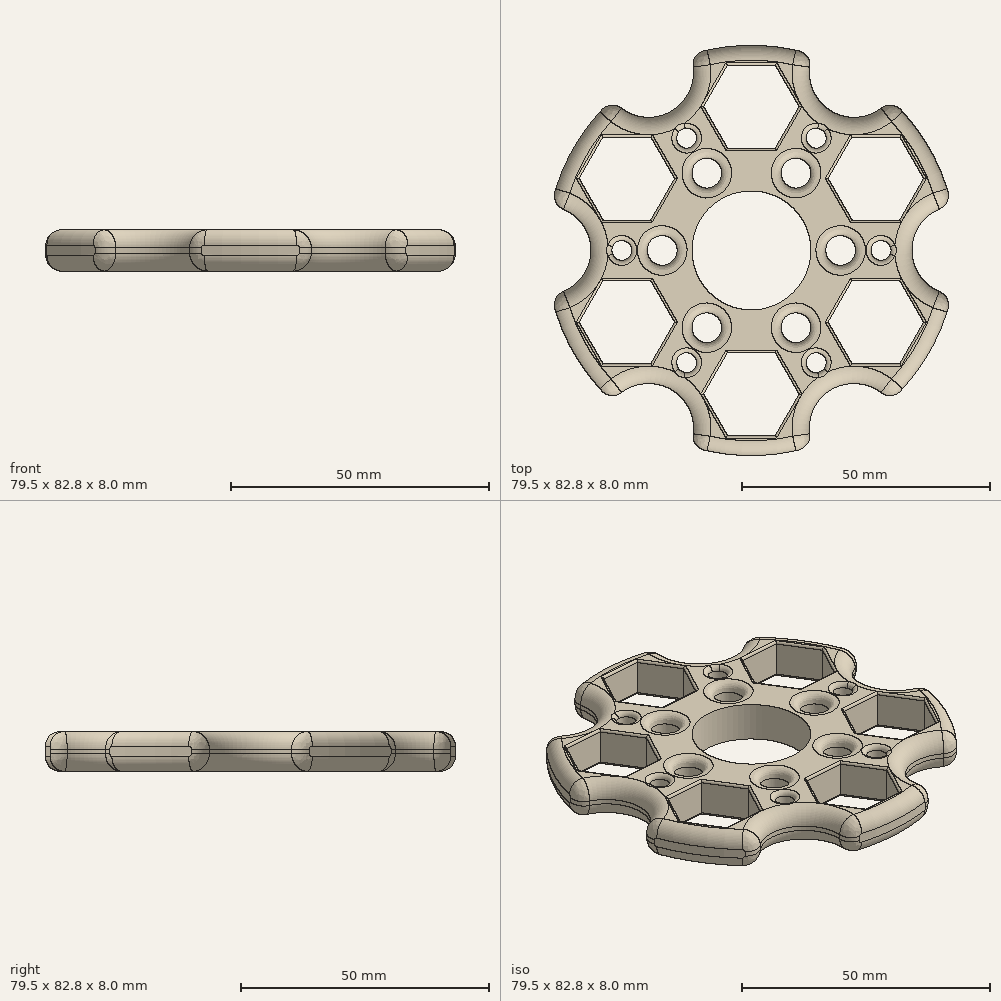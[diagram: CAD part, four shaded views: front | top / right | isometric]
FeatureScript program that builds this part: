
annotation { "Feature Type Name" : "Feature", "Feature Type Description" : "" }
export const myFeature = defineFeature(function(context is Context, id is Id, definition is map)
    precondition{}
    {
        {
            var Q0;
            Q0=qCreatedBy(makeId("Top.planeOp"),FACE);
            var sketch = newSketch(context, id + "F0", { "sketchPlane" : qUnion([Q0])});
            skCircle(sketch, "E0", {"center": v(0, 0) * mm, "radius": 12 * mm});
            skCircle(sketch, "E1", {"center": v(0, 0) * mm, "radius": 41.4 * mm});
            skCircle(sketch, "E2", {"center": v(0, 0) * mm, "radius": 29 * mm});
            skLineSegment(sketch, "E3", {"start": v(0, 0) * mm, "end": v(0, 47.75) * mm});
            skLineSegment(sketch, "E4", {"start": v(0, 0) * mm, "end": v(0, -67.46) * mm});
            skLineSegment(sketch, "E5", {"start": v(0, 0) * mm, "end": v(50.67, 29.25) * mm});
            skLineSegment(sketch, "E6", {"start": v(0, 0) * mm, "end": v(55.86, -32.25) * mm});
            skLineSegment(sketch, "E7", {"start": v(0, 0) * mm, "end": v(-57.52, -33.2) * mm});
            skLineSegment(sketch, "E8", {"start": v(0, 0) * mm, "end": v(-43.6, 25.17) * mm});
            skCircle(sketch, "E9.cCircle", {"center": v(0, 29) * mm, "radius": 8.35 * mm, "construction": true});
            skLineSegment(sketch, "E9.0", {"start": v(4.82, 20.65) * mm, "end": v(-4.82, 20.65) * mm});
            skLineSegment(sketch, "E9.1", {"start": v(-4.82, 20.65) * mm, "end": v(-9.64, 29) * mm});
            skLineSegment(sketch, "E9.2", {"start": v(-9.64, 29) * mm, "end": v(-4.82, 37.35) * mm});
            skLineSegment(sketch, "E9.3", {"start": v(-4.82, 37.35) * mm, "end": v(4.82, 37.35) * mm});
            skLineSegment(sketch, "E9.4", {"start": v(4.82, 37.35) * mm, "end": v(9.64, 29) * mm});
            skLineSegment(sketch, "E9.5", {"start": v(9.64, 29) * mm, "end": v(4.82, 20.65) * mm});
            skPoint(sketch, "E9.0.midPoint", {"position": v(0, 20.65) * mm});
            skCircle(sketch, "E10.cCircle", {"center": v(25.11, 14.5) * mm, "radius": 8.35 * mm, "construction": true});
            skLineSegment(sketch, "E10.0", {"start": v(20.3, 6.15) * mm, "end": v(15.47, 14.5) * mm});
            skLineSegment(sketch, "E10.1", {"start": v(15.47, 14.5) * mm, "end": v(20.3, 22.85) * mm});
            skLineSegment(sketch, "E10.2", {"start": v(20.3, 22.85) * mm, "end": v(29.94, 22.85) * mm});
            skLineSegment(sketch, "E10.3", {"start": v(29.94, 22.85) * mm, "end": v(34.76, 14.5) * mm});
            skLineSegment(sketch, "E10.4", {"start": v(34.76, 14.5) * mm, "end": v(29.94, 6.15) * mm});
            skLineSegment(sketch, "E10.5", {"start": v(29.94, 6.15) * mm, "end": v(20.3, 6.15) * mm});
            skPoint(sketch, "E10.0.midPoint", {"position": v(17.88, 10.33) * mm});
            skCircle(sketch, "E11.cCircle", {"center": v(25.11, -14.5) * mm, "radius": 8.35 * mm, "construction": true});
            skLineSegment(sketch, "E11.0", {"start": v(15.47, -14.5) * mm, "end": v(20.3, -6.15) * mm});
            skLineSegment(sketch, "E11.1", {"start": v(20.3, -6.15) * mm, "end": v(29.94, -6.15) * mm});
            skLineSegment(sketch, "E11.2", {"start": v(29.94, -6.15) * mm, "end": v(34.76, -14.5) * mm});
            skLineSegment(sketch, "E11.3", {"start": v(34.76, -14.5) * mm, "end": v(29.94, -22.85) * mm});
            skLineSegment(sketch, "E11.4", {"start": v(29.94, -22.85) * mm, "end": v(20.3, -22.85) * mm});
            skLineSegment(sketch, "E11.5", {"start": v(20.3, -22.85) * mm, "end": v(15.47, -14.5) * mm});
            skPoint(sketch, "E11.0.midPoint", {"position": v(17.88, -10.32) * mm});
            skCircle(sketch, "E12.cCircle", {"center": v(0, -29) * mm, "radius": 8.35 * mm, "construction": true});
            skLineSegment(sketch, "E12.0", {"start": v(-4.82, -20.65) * mm, "end": v(4.82, -20.65) * mm});
            skLineSegment(sketch, "E12.1", {"start": v(4.82, -20.65) * mm, "end": v(9.64, -29) * mm});
            skLineSegment(sketch, "E12.2", {"start": v(9.64, -29) * mm, "end": v(4.82, -37.35) * mm});
            skLineSegment(sketch, "E12.3", {"start": v(4.82, -37.35) * mm, "end": v(-4.82, -37.35) * mm});
            skLineSegment(sketch, "E12.4", {"start": v(-4.82, -37.35) * mm, "end": v(-9.64, -29) * mm});
            skLineSegment(sketch, "E12.5", {"start": v(-9.64, -29) * mm, "end": v(-4.82, -20.65) * mm});
            skPoint(sketch, "E12.0.midPoint", {"position": v(0, -20.65) * mm});
            skCircle(sketch, "E13.cCircle", {"center": v(-25.11, -14.5) * mm, "radius": 8.35 * mm, "construction": true});
            skLineSegment(sketch, "E13.0", {"start": v(-20.3, -6.15) * mm, "end": v(-15.47, -14.5) * mm});
            skLineSegment(sketch, "E13.1", {"start": v(-15.47, -14.5) * mm, "end": v(-20.3, -22.85) * mm});
            skLineSegment(sketch, "E13.2", {"start": v(-20.3, -22.85) * mm, "end": v(-29.94, -22.85) * mm});
            skLineSegment(sketch, "E13.3", {"start": v(-29.94, -22.85) * mm, "end": v(-34.76, -14.5) * mm});
            skLineSegment(sketch, "E13.4", {"start": v(-34.76, -14.5) * mm, "end": v(-29.94, -6.15) * mm});
            skLineSegment(sketch, "E13.5", {"start": v(-29.94, -6.15) * mm, "end": v(-20.3, -6.15) * mm});
            skPoint(sketch, "E13.0.midPoint", {"position": v(-17.88, -10.33) * mm});
            skCircle(sketch, "E14.cCircle", {"center": v(-25.11, 14.5) * mm, "radius": 8.35 * mm, "construction": true});
            skLineSegment(sketch, "E14.0", {"start": v(-15.47, 14.5) * mm, "end": v(-20.3, 6.15) * mm});
            skLineSegment(sketch, "E14.1", {"start": v(-20.3, 6.15) * mm, "end": v(-29.94, 6.15) * mm});
            skLineSegment(sketch, "E14.2", {"start": v(-29.94, 6.15) * mm, "end": v(-34.76, 14.5) * mm});
            skLineSegment(sketch, "E14.3", {"start": v(-34.76, 14.5) * mm, "end": v(-29.94, 22.85) * mm});
            skLineSegment(sketch, "E14.4", {"start": v(-29.94, 22.85) * mm, "end": v(-20.3, 22.85) * mm});
            skLineSegment(sketch, "E14.5", {"start": v(-20.3, 22.85) * mm, "end": v(-15.47, 14.5) * mm});
            skPoint(sketch, "E14.0.midPoint", {"position": v(-17.88, 10.32) * mm});
            skLineSegment(sketch, "E15", {"start": v(0, 0) * mm, "end": v(-28.15, -48.76) * mm});
            skLineSegment(sketch, "E16", {"start": v(0, 0) * mm, "end": v(-26.9, 46.6) * mm});
            skLineSegment(sketch, "E17", {"start": v(0, 0) * mm, "end": v(-57.79, 0) * mm});
            skLineSegment(sketch, "E18", {"start": v(0, 0) * mm, "end": v(54.8, 0) * mm});
            skLineSegment(sketch, "E19", {"start": v(0, 0) * mm, "end": v(27, -46.77) * mm});
            skLineSegment(sketch, "E20", {"start": v(0, 0) * mm, "end": v(25.69, 44.49) * mm});
            skCircle(sketch, "E21", {"center": v(-20.7, 35.85) * mm, "radius": 9 * mm});
            skCircle(sketch, "E22", {"center": v(41.4, 0) * mm, "radius": 9 * mm});
            skCircle(sketch, "E23", {"center": v(20.7, 35.85) * mm, "radius": 9 * mm});
            skCircle(sketch, "E24", {"center": v(20.7, -35.85) * mm, "radius": 9 * mm});
            skCircle(sketch, "E25", {"center": v(-20.7, -35.85) * mm, "radius": 9 * mm});
            skCircle(sketch, "E26", {"center": v(-41.4, 0) * mm, "radius": 9 * mm});
            skCircle(sketch, "E27", {"center": v(0, 0) * mm, "radius": 18 * mm});
            skCircle(sketch, "E28", {"center": v(-18, 0) * mm, "radius": 3 * mm});
            skCircle(sketch, "E29", {"center": v(-9, 15.59) * mm, "radius": 3 * mm});
            skCircle(sketch, "E30", {"center": v(9, 15.59) * mm, "radius": 3 * mm});
            skCircle(sketch, "E31", {"center": v(18, 0) * mm, "radius": 3 * mm});
            skCircle(sketch, "E32", {"center": v(9, -15.59) * mm, "radius": 3 * mm});
            skCircle(sketch, "E33", {"center": v(-9, -15.59) * mm, "radius": 3 * mm});
            skCircle(sketch, "E34", {"center": v(0, 0) * mm, "radius": 26.15 * mm});
            skCircle(sketch, "E35", {"center": v(-13.08, -22.65) * mm, "radius": 2 * mm});
            skCircle(sketch, "E36", {"center": v(13.08, -22.65) * mm, "radius": 2 * mm});
            skCircle(sketch, "E37", {"center": v(26.15, 0) * mm, "radius": 2 * mm});
            skCircle(sketch, "E38", {"center": v(13.08, 22.65) * mm, "radius": 2 * mm});
            skCircle(sketch, "E39", {"center": v(-13.08, 22.65) * mm, "radius": 2 * mm});
            skCircle(sketch, "E40", {"center": v(-26.15, 0) * mm, "radius": 2 * mm});
            skSolve(sketch);
        }
        {
            var Q0;
            {var subQ0=sQuery(id+"F0.wireOp",EDGE,"E10.4");Q0=makeQuery(id+"F0.imprint","IMPRINT",FACE,{"disambiguationData":[TD([[makeQuery(id+"F0.imprint","IMPRINT",EDGE,{"derivedFrom":subQ0}),1.0]])]});}
            var Q1;
            {var subQ5=sQuery(id+"F0.wireOp",EDGE,"E10.2");Q1=makeQuery(id+"F0.imprint","IMPRINT",FACE,{"disambiguationData":[TD([[makeQuery(id+"F0.imprint","IMPRINT",EDGE,{"derivedFrom":subQ5}),1.0]])]});}
            var Q2;
            {var subQ10=sQuery(id+"F0.wireOp",EDGE,"E9.4");Q2=makeQuery(id+"F0.imprint","IMPRINT",FACE,{"disambiguationData":[TD([[makeQuery(id+"F0.imprint","IMPRINT",EDGE,{"derivedFrom":subQ10}),1.0]])]});}
            var Q3;
            {var subQ0=sQuery(id+"F0.wireOp",EDGE,"E9.2");Q3=makeQuery(id+"F0.imprint","IMPRINT",FACE,{"disambiguationData":[TD([[makeQuery(id+"F0.imprint","IMPRINT",EDGE,{"derivedFrom":subQ0}),1.0]])]});}
            var Q4;
            {var subQ0=sQuery(id+"F0.wireOp",EDGE,"E14.4");Q4=makeQuery(id+"F0.imprint","IMPRINT",FACE,{"disambiguationData":[TD([[makeQuery(id+"F0.imprint","IMPRINT",EDGE,{"derivedFrom":subQ0}),1.0]])]});}
            var Q5;
            {var subQ0=sQuery(id+"F0.wireOp",EDGE,"E14.2");Q5=makeQuery(id+"F0.imprint","IMPRINT",FACE,{"disambiguationData":[TD([[makeQuery(id+"F0.imprint","IMPRINT",EDGE,{"derivedFrom":subQ0}),1.0]])]});}
            var Q6;
            {var subQ0=sQuery(id+"F0.wireOp",EDGE,"E13.4");Q6=makeQuery(id+"F0.imprint","IMPRINT",FACE,{"disambiguationData":[TD([[makeQuery(id+"F0.imprint","IMPRINT",EDGE,{"derivedFrom":subQ0}),1.0]])]});}
            var Q7;
            {var subQ0=sQuery(id+"F0.wireOp",EDGE,"E13.2");Q7=makeQuery(id+"F0.imprint","IMPRINT",FACE,{"disambiguationData":[TD([[makeQuery(id+"F0.imprint","IMPRINT",EDGE,{"derivedFrom":subQ0}),1.0]])]});}
            var Q8;
            {var subQ5=sQuery(id+"F0.wireOp",EDGE,"E12.4");Q8=makeQuery(id+"F0.imprint","IMPRINT",FACE,{"disambiguationData":[TD([[makeQuery(id+"F0.imprint","IMPRINT",EDGE,{"derivedFrom":subQ5}),1.0]])]});}
            var Q9;
            {var subQ0=sQuery(id+"F0.wireOp",EDGE,"E12.2");Q9=makeQuery(id+"F0.imprint","IMPRINT",FACE,{"disambiguationData":[TD([[makeQuery(id+"F0.imprint","IMPRINT",EDGE,{"derivedFrom":subQ0}),1.0]])]});}
            var Q10;
            {var subQ0=sQuery(id+"F0.wireOp",EDGE,"E11.4");Q10=makeQuery(id+"F0.imprint","IMPRINT",FACE,{"disambiguationData":[TD([[makeQuery(id+"F0.imprint","IMPRINT",EDGE,{"derivedFrom":subQ0}),1.0]])]});}
            var Q11;
            {var subQ5=sQuery(id+"F0.wireOp",EDGE,"E11.2");Q11=makeQuery(id+"F0.imprint","IMPRINT",FACE,{"disambiguationData":[TD([[makeQuery(id+"F0.imprint","IMPRINT",EDGE,{"derivedFrom":subQ5}),1.0]])]});}
            var Q12;
            {var subQ0=sQuery(id+"F0.wireOp",EDGE,"E17");var subQ1=sQuery(id+"F0.wireOp",EDGE,"E0");var subQ2=makeQuery(id+"F0.imprint","INTERSECT",VERTEX,{"derivedFrom":[subQ1,subQ0]});Q12=makeQuery(id+"F0.imprint","IMPRINT",FACE,{"disambiguationData":[TD([[makeQuery(id+"F0.imprint","IMPRINT",EDGE,{"disambiguationData":[TD([[subQ2,-1.0]])],"derivedFrom":subQ1}),-1.0]])]});}
            var Q13;
            {var subQ5=sQuery(id+"F0.wireOp",EDGE,"E16");var subQ6=sQuery(id+"F0.wireOp",EDGE,"E0");var subQ7=makeQuery(id+"F0.imprint","INTERSECT",VERTEX,{"derivedFrom":[subQ6,subQ5]});Q13=makeQuery(id+"F0.imprint","IMPRINT",FACE,{"disambiguationData":[TD([[makeQuery(id+"F0.imprint","IMPRINT",EDGE,{"disambiguationData":[TD([[subQ7,-1.0]])],"derivedFrom":subQ6}),-1.0]])]});}
            var Q14;
            {var subQ1=sQuery(id+"F0.wireOp",EDGE,"E8");var subQ6=sQuery(id+"F0.wireOp",EDGE,"E0");var subQ9=makeQuery(id+"F0.imprint","INTERSECT",VERTEX,{"derivedFrom":[subQ6,subQ1]});Q14=makeQuery(id+"F0.imprint","IMPRINT",FACE,{"disambiguationData":[TD([[makeQuery(id+"F0.imprint","IMPRINT",EDGE,{"disambiguationData":[TD([[subQ9,-1.0]])],"derivedFrom":subQ6}),-1.0]])]});}
            var Q15;
            {var subQ3=sQuery(id+"F0.wireOp",EDGE,"E2");var subQ7=sQuery(id+"F0.wireOp",EDGE,"E16");var subQ8=makeQuery(id+"F0.imprint","INTERSECT",VERTEX,{"derivedFrom":[subQ3,subQ7]});Q15=makeQuery(id+"F0.imprint","IMPRINT",FACE,{"disambiguationData":[TD([[makeQuery(id+"F0.imprint","IMPRINT",EDGE,{"disambiguationData":[TD([[subQ8,-1.0]])],"derivedFrom":subQ3}),1.0]])]});}
            var Q16;
            {var subQ0=sQuery(id+"F0.wireOp",EDGE,"E9.1");var subQ7=sQuery(id+"F0.wireOp",EDGE,"E2");var subQ8=makeQuery(id+"F0.imprint","INTERSECT",VERTEX,{"derivedFrom":[subQ7,subQ0]});Q16=makeQuery(id+"F0.imprint","IMPRINT",FACE,{"disambiguationData":[TD([[makeQuery(id+"F0.imprint","IMPRINT",EDGE,{"disambiguationData":[TD([[subQ8,-1.0]])],"derivedFrom":subQ7}),1.0]])]});}
            var Q17;
            {var subQ1=sQuery(id+"F0.wireOp",EDGE,"E3");var subQ5=sQuery(id+"F0.wireOp",EDGE,"E0");var subQ6=makeQuery(id+"F0.imprint","INTERSECT",VERTEX,{"derivedFrom":[subQ5,subQ1]});Q17=makeQuery(id+"F0.imprint","IMPRINT",FACE,{"disambiguationData":[TD([[makeQuery(id+"F0.imprint","IMPRINT",EDGE,{"disambiguationData":[TD([[subQ6,-1.0]])],"derivedFrom":subQ5}),-1.0]])]});}
            var Q18;
            {var subQ5=sQuery(id+"F0.wireOp",EDGE,"E20");var subQ6=sQuery(id+"F0.wireOp",EDGE,"E0");var subQ7=makeQuery(id+"F0.imprint","INTERSECT",VERTEX,{"derivedFrom":[subQ6,subQ5]});Q18=makeQuery(id+"F0.imprint","IMPRINT",FACE,{"disambiguationData":[TD([[makeQuery(id+"F0.imprint","IMPRINT",EDGE,{"disambiguationData":[TD([[subQ7,-1.0]])],"derivedFrom":subQ6}),-1.0]])]});}
            var Q19;
            {var subQ7=sQuery(id+"F0.wireOp",EDGE,"E20");var subQ8=sQuery(id+"F0.wireOp",EDGE,"E2");var subQ9=makeQuery(id+"F0.imprint","INTERSECT",VERTEX,{"derivedFrom":[subQ8,subQ7]});Q19=makeQuery(id+"F0.imprint","IMPRINT",FACE,{"disambiguationData":[TD([[makeQuery(id+"F0.imprint","IMPRINT",EDGE,{"disambiguationData":[TD([[subQ9,-1.0]])],"derivedFrom":subQ8}),1.0]])]});}
            var Q20;
            {var subQ0=sQuery(id+"F0.wireOp",EDGE,"E10.1");var subQ3=sQuery(id+"F0.wireOp",EDGE,"E2");var subQ4=makeQuery(id+"F0.imprint","INTERSECT",VERTEX,{"derivedFrom":[subQ3,subQ0]});Q20=makeQuery(id+"F0.imprint","IMPRINT",FACE,{"disambiguationData":[TD([[makeQuery(id+"F0.imprint","IMPRINT",EDGE,{"disambiguationData":[TD([[subQ4,-1.0]])],"derivedFrom":subQ3}),1.0]])]});}
            var Q21;
            {var subQ1=sQuery(id+"F0.wireOp",EDGE,"E5");var subQ6=sQuery(id+"F0.wireOp",EDGE,"E0");var subQ9=makeQuery(id+"F0.imprint","INTERSECT",VERTEX,{"derivedFrom":[subQ6,subQ1]});Q21=makeQuery(id+"F0.imprint","IMPRINT",FACE,{"disambiguationData":[TD([[makeQuery(id+"F0.imprint","IMPRINT",EDGE,{"disambiguationData":[TD([[subQ9,-1.0]])],"derivedFrom":subQ6}),-1.0]])]});}
            var Q22;
            {var subQ1=sQuery(id+"F0.wireOp",EDGE,"E5");var subQ6=sQuery(id+"F0.wireOp",EDGE,"E0");var subQ9=makeQuery(id+"F0.imprint","INTERSECT",VERTEX,{"derivedFrom":[subQ6,subQ1]});Q22=makeQuery(id+"F0.imprint","IMPRINT",FACE,{"disambiguationData":[TD([[makeQuery(id+"F0.imprint","IMPRINT",EDGE,{"disambiguationData":[TD([[subQ9,1.0]])],"derivedFrom":subQ6}),-1.0]])]});}
            var Q23;
            {var subQ5=sQuery(id+"F0.wireOp",EDGE,"E0");var subQ7=sQuery(id+"F0.wireOp",EDGE,"E18");var subQ9=makeQuery(id+"F0.imprint","INTERSECT",VERTEX,{"derivedFrom":[subQ5,subQ7]});Q23=makeQuery(id+"F0.imprint","IMPRINT",FACE,{"disambiguationData":[TD([[makeQuery(id+"F0.imprint","IMPRINT",EDGE,{"disambiguationData":[TD([[subQ9,1.0]])],"derivedFrom":subQ5}),-1.0]])]});}
            var Q24;
            {var subQ5=sQuery(id+"F0.wireOp",EDGE,"E19");var subQ6=sQuery(id+"F0.wireOp",EDGE,"E0");var subQ7=makeQuery(id+"F0.imprint","INTERSECT",VERTEX,{"derivedFrom":[subQ6,subQ5]});Q24=makeQuery(id+"F0.imprint","IMPRINT",FACE,{"disambiguationData":[TD([[makeQuery(id+"F0.imprint","IMPRINT",EDGE,{"disambiguationData":[TD([[subQ7,-1.0]])],"derivedFrom":subQ6}),-1.0]])]});}
            var Q25;
            {var subQ1=sQuery(id+"F0.wireOp",EDGE,"E4");var subQ5=sQuery(id+"F0.wireOp",EDGE,"E0");var subQ6=makeQuery(id+"F0.imprint","INTERSECT",VERTEX,{"derivedFrom":[subQ5,subQ1]});Q25=makeQuery(id+"F0.imprint","IMPRINT",FACE,{"disambiguationData":[TD([[makeQuery(id+"F0.imprint","IMPRINT",EDGE,{"disambiguationData":[TD([[subQ6,-1.0]])],"derivedFrom":subQ5}),-1.0]])]});}
            var Q26;
            {var subQ5=sQuery(id+"F0.wireOp",EDGE,"E15");var subQ6=sQuery(id+"F0.wireOp",EDGE,"E0");var subQ7=makeQuery(id+"F0.imprint","INTERSECT",VERTEX,{"derivedFrom":[subQ6,subQ5]});Q26=makeQuery(id+"F0.imprint","IMPRINT",FACE,{"disambiguationData":[TD([[makeQuery(id+"F0.imprint","IMPRINT",EDGE,{"disambiguationData":[TD([[subQ7,-1.0]])],"derivedFrom":subQ6}),-1.0]])]});}
            var Q27;
            {var subQ0=sQuery(id+"F0.wireOp",EDGE,"E7");var subQ1=sQuery(id+"F0.wireOp",EDGE,"E0");var subQ2=makeQuery(id+"F0.imprint","INTERSECT",VERTEX,{"derivedFrom":[subQ1,subQ0]});Q27=makeQuery(id+"F0.imprint","IMPRINT",FACE,{"disambiguationData":[TD([[makeQuery(id+"F0.imprint","IMPRINT",EDGE,{"disambiguationData":[TD([[subQ2,-1.0]])],"derivedFrom":subQ1}),-1.0]])]});}
            var Q28;
            {var subQ0=sQuery(id+"F0.wireOp",EDGE,"E13.1");var subQ3=sQuery(id+"F0.wireOp",EDGE,"E2");var subQ4=makeQuery(id+"F0.imprint","INTERSECT",VERTEX,{"derivedFrom":[subQ3,subQ0]});Q28=makeQuery(id+"F0.imprint","IMPRINT",FACE,{"disambiguationData":[TD([[makeQuery(id+"F0.imprint","IMPRINT",EDGE,{"disambiguationData":[TD([[subQ4,-1.0]])],"derivedFrom":subQ3}),1.0]])]});}
            var Q29;
            {var subQ3=sQuery(id+"F0.wireOp",EDGE,"E2");var subQ11=sQuery(id+"F0.wireOp",EDGE,"E15");var subQ12=makeQuery(id+"F0.imprint","INTERSECT",VERTEX,{"derivedFrom":[subQ3,subQ11]});Q29=makeQuery(id+"F0.imprint","IMPRINT",FACE,{"disambiguationData":[TD([[makeQuery(id+"F0.imprint","IMPRINT",EDGE,{"disambiguationData":[TD([[subQ12,-1.0]])],"derivedFrom":subQ3}),1.0]])]});}
            var Q30;
            {var subQ0=sQuery(id+"F0.wireOp",EDGE,"E12.1");var subQ10=sQuery(id+"F0.wireOp",EDGE,"E2");var subQ11=makeQuery(id+"F0.imprint","INTERSECT",VERTEX,{"derivedFrom":[subQ10,subQ0]});Q30=makeQuery(id+"F0.imprint","IMPRINT",FACE,{"disambiguationData":[TD([[makeQuery(id+"F0.imprint","IMPRINT",EDGE,{"disambiguationData":[TD([[subQ11,-1.0]])],"derivedFrom":subQ10}),1.0]])]});}
            var Q31;
            {var subQ3=sQuery(id+"F0.wireOp",EDGE,"E2");var subQ9=sQuery(id+"F0.wireOp",EDGE,"E19");var subQ10=makeQuery(id+"F0.imprint","INTERSECT",VERTEX,{"derivedFrom":[subQ3,subQ9]});Q31=makeQuery(id+"F0.imprint","IMPRINT",FACE,{"disambiguationData":[TD([[makeQuery(id+"F0.imprint","IMPRINT",EDGE,{"disambiguationData":[TD([[subQ10,-1.0]])],"derivedFrom":subQ3}),1.0]])]});}
            var Q32;
            {var subQ3=sQuery(id+"F0.wireOp",EDGE,"E2");var subQ5=sQuery(id+"F0.wireOp",EDGE,"E18");var subQ6=makeQuery(id+"F0.imprint","INTERSECT",VERTEX,{"derivedFrom":[subQ3,subQ5]});Q32=makeQuery(id+"F0.imprint","IMPRINT",FACE,{"disambiguationData":[TD([[makeQuery(id+"F0.imprint","IMPRINT",EDGE,{"disambiguationData":[TD([[subQ6,1.0]])],"derivedFrom":subQ3}),1.0]])]});}
            var Q33;
            {var subQ0=sQuery(id+"F0.wireOp",EDGE,"E10.5");var subQ3=sQuery(id+"F0.wireOp",EDGE,"E2");var subQ4=makeQuery(id+"F0.imprint","INTERSECT",VERTEX,{"derivedFrom":[subQ3,subQ0]});Q33=makeQuery(id+"F0.imprint","IMPRINT",FACE,{"disambiguationData":[TD([[makeQuery(id+"F0.imprint","IMPRINT",EDGE,{"disambiguationData":[TD([[subQ4,1.0]])],"derivedFrom":subQ3}),1.0]])]});}
            var Q34;
            {var subQ3=sQuery(id+"F0.wireOp",EDGE,"E2");var subQ7=sQuery(id+"F0.wireOp",EDGE,"E17");var subQ8=makeQuery(id+"F0.imprint","INTERSECT",VERTEX,{"derivedFrom":[subQ3,subQ7]});Q34=makeQuery(id+"F0.imprint","IMPRINT",FACE,{"disambiguationData":[TD([[makeQuery(id+"F0.imprint","IMPRINT",EDGE,{"disambiguationData":[TD([[subQ8,-1.0]])],"derivedFrom":subQ3}),1.0]])]});}
            var Q35;
            {var subQ0=sQuery(id+"F0.wireOp",EDGE,"E14.1");var subQ3=sQuery(id+"F0.wireOp",EDGE,"E2");var subQ4=makeQuery(id+"F0.imprint","INTERSECT",VERTEX,{"derivedFrom":[subQ3,subQ0]});Q35=makeQuery(id+"F0.imprint","IMPRINT",FACE,{"disambiguationData":[TD([[makeQuery(id+"F0.imprint","IMPRINT",EDGE,{"disambiguationData":[TD([[subQ4,-1.0]])],"derivedFrom":subQ3}),1.0]])]});}
            var Q36;
            {var subQ5=sQuery(id+"F0.wireOp",EDGE,"E27");var subQ6=sQuery(id+"F0.wireOp",EDGE,"E7");var subQ7=makeQuery(id+"F0.imprint","INTERSECT",VERTEX,{"derivedFrom":[subQ6,subQ5]});Q36=makeQuery(id+"F0.imprint","IMPRINT",FACE,{"disambiguationData":[TD([[makeQuery(id+"F0.imprint","IMPRINT",EDGE,{"disambiguationData":[TD([[subQ7,-1.0]])],"derivedFrom":subQ6}),1.0]])]});}
            var Q37;
            {var subQ5=sQuery(id+"F0.wireOp",EDGE,"E27");var subQ10=sQuery(id+"F0.wireOp",EDGE,"E4");var subQ14=makeQuery(id+"F0.imprint","INTERSECT",VERTEX,{"derivedFrom":[subQ10,subQ5]});Q37=makeQuery(id+"F0.imprint","IMPRINT",FACE,{"disambiguationData":[TD([[makeQuery(id+"F0.imprint","IMPRINT",EDGE,{"disambiguationData":[TD([[subQ14,-1.0]])],"derivedFrom":subQ10}),-1.0]])]});}
            var Q38;
            {var subQ11=sQuery(id+"F0.wireOp",EDGE,"E6");var subQ13=sQuery(id+"F0.wireOp",EDGE,"E27");var subQ14=makeQuery(id+"F0.imprint","INTERSECT",VERTEX,{"derivedFrom":[subQ11,subQ13]});Q38=makeQuery(id+"F0.imprint","IMPRINT",FACE,{"disambiguationData":[TD([[makeQuery(id+"F0.imprint","IMPRINT",EDGE,{"disambiguationData":[TD([[subQ14,-1.0]])],"derivedFrom":subQ11}),-1.0]])]});}
            var Q39;
            {var subQ8=sQuery(id+"F0.wireOp",EDGE,"E6");var subQ10=sQuery(id+"F0.wireOp",EDGE,"E27");var subQ11=makeQuery(id+"F0.imprint","INTERSECT",VERTEX,{"derivedFrom":[subQ8,subQ10]});Q39=makeQuery(id+"F0.imprint","IMPRINT",FACE,{"disambiguationData":[TD([[makeQuery(id+"F0.imprint","IMPRINT",EDGE,{"disambiguationData":[TD([[subQ11,-1.0]])],"derivedFrom":subQ8}),1.0]])]});}
            var Q40;
            {var subQ5=sQuery(id+"F0.wireOp",EDGE,"E5");var subQ12=sQuery(id+"F0.wireOp",EDGE,"E27");var subQ13=makeQuery(id+"F0.imprint","INTERSECT",VERTEX,{"derivedFrom":[subQ5,subQ12]});Q40=makeQuery(id+"F0.imprint","IMPRINT",FACE,{"disambiguationData":[TD([[makeQuery(id+"F0.imprint","IMPRINT",EDGE,{"disambiguationData":[TD([[subQ13,-1.0]])],"derivedFrom":subQ5}),-1.0]])]});}
            var Q41;
            {var subQ5=sQuery(id+"F0.wireOp",EDGE,"E27");var subQ6=sQuery(id+"F0.wireOp",EDGE,"E5");var subQ7=makeQuery(id+"F0.imprint","INTERSECT",VERTEX,{"derivedFrom":[subQ6,subQ5]});Q41=makeQuery(id+"F0.imprint","IMPRINT",FACE,{"disambiguationData":[TD([[makeQuery(id+"F0.imprint","IMPRINT",EDGE,{"disambiguationData":[TD([[subQ7,-1.0]])],"derivedFrom":subQ6}),1.0]])]});}
            var Q42;
            {var subQ10=sQuery(id+"F0.wireOp",EDGE,"E3");var subQ12=sQuery(id+"F0.wireOp",EDGE,"E27");var subQ13=makeQuery(id+"F0.imprint","INTERSECT",VERTEX,{"derivedFrom":[subQ10,subQ12]});Q42=makeQuery(id+"F0.imprint","IMPRINT",FACE,{"disambiguationData":[TD([[makeQuery(id+"F0.imprint","IMPRINT",EDGE,{"disambiguationData":[TD([[subQ13,-1.0]])],"derivedFrom":subQ10}),-1.0]])]});}
            var Q43;
            {var subQ10=sQuery(id+"F0.wireOp",EDGE,"E3");var subQ13=sQuery(id+"F0.wireOp",EDGE,"E27");var subQ14=makeQuery(id+"F0.imprint","INTERSECT",VERTEX,{"derivedFrom":[subQ10,subQ13]});Q43=makeQuery(id+"F0.imprint","IMPRINT",FACE,{"disambiguationData":[TD([[makeQuery(id+"F0.imprint","IMPRINT",EDGE,{"disambiguationData":[TD([[subQ14,-1.0]])],"derivedFrom":subQ10}),1.0]])]});}
            var Q44;
            {var subQ10=sQuery(id+"F0.wireOp",EDGE,"E8");var subQ12=sQuery(id+"F0.wireOp",EDGE,"E27");var subQ13=makeQuery(id+"F0.imprint","INTERSECT",VERTEX,{"derivedFrom":[subQ10,subQ12]});Q44=makeQuery(id+"F0.imprint","IMPRINT",FACE,{"disambiguationData":[TD([[makeQuery(id+"F0.imprint","IMPRINT",EDGE,{"disambiguationData":[TD([[subQ13,-1.0]])],"derivedFrom":subQ10}),-1.0]])]});}
            var Q45;
            {var subQ10=sQuery(id+"F0.wireOp",EDGE,"E27");var subQ11=sQuery(id+"F0.wireOp",EDGE,"E8");var subQ12=makeQuery(id+"F0.imprint","INTERSECT",VERTEX,{"derivedFrom":[subQ11,subQ10]});Q45=makeQuery(id+"F0.imprint","IMPRINT",FACE,{"disambiguationData":[TD([[makeQuery(id+"F0.imprint","IMPRINT",EDGE,{"disambiguationData":[TD([[subQ12,-1.0]])],"derivedFrom":subQ11}),1.0]])]});}
            var Q46;
            {var subQ5=sQuery(id+"F0.wireOp",EDGE,"E7");var subQ12=sQuery(id+"F0.wireOp",EDGE,"E27");var subQ13=makeQuery(id+"F0.imprint","INTERSECT",VERTEX,{"derivedFrom":[subQ5,subQ12]});Q46=makeQuery(id+"F0.imprint","IMPRINT",FACE,{"disambiguationData":[TD([[makeQuery(id+"F0.imprint","IMPRINT",EDGE,{"disambiguationData":[TD([[subQ13,-1.0]])],"derivedFrom":subQ5}),-1.0]])]});}
            var Q47;
            {var subQ10=sQuery(id+"F0.wireOp",EDGE,"E4");var subQ12=sQuery(id+"F0.wireOp",EDGE,"E27");var subQ13=makeQuery(id+"F0.imprint","INTERSECT",VERTEX,{"derivedFrom":[subQ10,subQ12]});Q47=makeQuery(id+"F0.imprint","IMPRINT",FACE,{"disambiguationData":[TD([[makeQuery(id+"F0.imprint","IMPRINT",EDGE,{"disambiguationData":[TD([[subQ13,-1.0]])],"derivedFrom":subQ10}),1.0]])]});}
            extrude(context, id + "F1", {"entities" : qUnion([Q0, Q1, Q2, Q3, Q4, Q5, Q6, Q7, Q8, Q9, Q10, Q11, Q12, Q13, Q14, Q15, Q16, Q17, Q18, Q19, Q20, Q21, Q22, Q23, Q24, Q25, Q26, Q27, Q28, Q29, Q30, Q31, Q32, Q33, Q34, Q35, Q36, Q37, Q38, Q39, Q40, Q41, Q42, Q43, Q44, Q45, Q46, Q47]), "depth" : 8 * mm, "offsetDistance" : 25 * mm});
        }
        {
            var Q0;
            Q0=makeQuery(id+"F1.opExtrude","CAP_EDGE",EDGE,{"disambiguationData":[OSD([sQuery(id+"F0.wireOp",EDGE,"E21")])],"isStart":false});
            var Q1;
            Q1=makeQuery(id+"F1.opExtrude","CAP_EDGE",EDGE,{"disambiguationData":[OSD([sQuery(id+"F0.wireOp",EDGE,"E23")])],"isStart":false});
            var Q2;
            Q2=makeQuery(id+"F1.opExtrude","CAP_EDGE",EDGE,{"disambiguationData":[OSD([sQuery(id+"F0.wireOp",EDGE,"E22")])],"isStart":false});
            var Q3;
            Q3=makeQuery(id+"F1.opExtrude","CAP_EDGE",EDGE,{"disambiguationData":[OSD([sQuery(id+"F0.wireOp",EDGE,"E24")])],"isStart":false});
            var Q4;
            Q4=makeQuery(id+"F1.opExtrude","CAP_EDGE",EDGE,{"disambiguationData":[OSD([sQuery(id+"F0.wireOp",EDGE,"E25")])],"isStart":false});
            var Q5;
            Q5=makeQuery(id+"F1.opExtrude","CAP_EDGE",EDGE,{"disambiguationData":[OSD([sQuery(id+"F0.wireOp",EDGE,"E26")])],"isStart":false});
            var Q6;
            Q6=makeQuery(id+"F1.opExtrude","CAP_EDGE",EDGE,{"disambiguationData":[OSD([sQuery(id+"F0.wireOp",EDGE,"E23")])],"isStart":true});
            var Q7;
            Q7=makeQuery(id+"F1.opExtrude","CAP_EDGE",EDGE,{"disambiguationData":[OSD([sQuery(id+"F0.wireOp",EDGE,"E22")])],"isStart":true});
            var Q8;
            Q8=makeQuery(id+"F1.opExtrude","CAP_EDGE",EDGE,{"disambiguationData":[OSD([sQuery(id+"F0.wireOp",EDGE,"E24")])],"isStart":true});
            var Q9;
            Q9=makeQuery(id+"F1.opExtrude","CAP_EDGE",EDGE,{"disambiguationData":[OSD([sQuery(id+"F0.wireOp",EDGE,"E25")])],"isStart":true});
            var Q10;
            Q10=makeQuery(id+"F1.opExtrude","CAP_EDGE",EDGE,{"disambiguationData":[OSD([sQuery(id+"F0.wireOp",EDGE,"E26")])],"isStart":true});
            var Q11;
            Q11=makeQuery(id+"F1.opExtrude","CAP_EDGE",EDGE,{"disambiguationData":[OSD([sQuery(id+"F0.wireOp",EDGE,"E21")])],"isStart":true});
            fillet(context, id + "F2", {"entities" : qUnion([Q0, Q1, Q2, Q3, Q4, Q5, Q6, Q7, Q8, Q9, Q10, Q11]), "radius" : 3.5 * mm, "tangentPropagation" : true, "allowEdgeOverflow" : false});
        }
        {
            var Q0;
            Q0=makeQuery(id+"F1.opExtrude","CAP_EDGE",EDGE,{"disambiguationData":[OSD([sQuery(id+"F0.wireOp",EDGE,"E33")])],"isStart":false});
            var Q1;
            Q1=makeQuery(id+"F1.opExtrude","CAP_EDGE",EDGE,{"disambiguationData":[OSD([sQuery(id+"F0.wireOp",EDGE,"E28")])],"isStart":false});
            var Q2;
            Q2=makeQuery(id+"F1.opExtrude","CAP_EDGE",EDGE,{"disambiguationData":[OSD([sQuery(id+"F0.wireOp",EDGE,"E29")])],"isStart":false});
            var Q3;
            Q3=makeQuery(id+"F1.opExtrude","CAP_EDGE",EDGE,{"disambiguationData":[OSD([sQuery(id+"F0.wireOp",EDGE,"E30")])],"isStart":false});
            var Q4;
            Q4=makeQuery(id+"F1.opExtrude","CAP_EDGE",EDGE,{"disambiguationData":[OSD([sQuery(id+"F0.wireOp",EDGE,"E31")])],"isStart":false});
            var Q5;
            Q5=makeQuery(id+"F1.opExtrude","CAP_EDGE",EDGE,{"disambiguationData":[OSD([sQuery(id+"F0.wireOp",EDGE,"E32")])],"isStart":false});
            var Q6;
            Q6=makeQuery(id+"F1.opExtrude","CAP_EDGE",EDGE,{"disambiguationData":[OSD([sQuery(id+"F0.wireOp",EDGE,"E28")])],"isStart":true});
            var Q7;
            Q7=makeQuery(id+"F1.opExtrude","CAP_EDGE",EDGE,{"disambiguationData":[OSD([sQuery(id+"F0.wireOp",EDGE,"E29")])],"isStart":true});
            var Q8;
            Q8=makeQuery(id+"F1.opExtrude","CAP_EDGE",EDGE,{"disambiguationData":[OSD([sQuery(id+"F0.wireOp",EDGE,"E30")])],"isStart":true});
            var Q9;
            Q9=makeQuery(id+"F1.opExtrude","CAP_EDGE",EDGE,{"disambiguationData":[OSD([sQuery(id+"F0.wireOp",EDGE,"E31")])],"isStart":true});
            var Q10;
            Q10=makeQuery(id+"F1.opExtrude","CAP_EDGE",EDGE,{"disambiguationData":[OSD([sQuery(id+"F0.wireOp",EDGE,"E32")])],"isStart":true});
            var Q11;
            Q11=makeQuery(id+"F1.opExtrude","CAP_EDGE",EDGE,{"disambiguationData":[OSD([sQuery(id+"F0.wireOp",EDGE,"E33")])],"isStart":true});
            fillet(context, id + "F3", {"entities" : qUnion([Q0, Q1, Q2, Q3, Q4, Q5, Q6, Q7, Q8, Q9, Q10, Q11]), "radius" : 2 * mm, "tangentPropagation" : true, "rho" : 0.5, "crossSection" : FilletCrossSection.CONIC, "allowEdgeOverflow" : false});
        }
        {
            var Q0;
            Q0=makeQuery(id+"F1.opExtrude","CAP_EDGE",EDGE,{"disambiguationData":[OSD([sQuery(id+"F0.wireOp",EDGE,"E14.2")])],"isStart":false});
            var Q1;
            Q1=makeQuery(id+"F1.opExtrude","CAP_EDGE",EDGE,{"disambiguationData":[OSD([sQuery(id+"F0.wireOp",EDGE,"E14.3")])],"isStart":false});
            var Q2;
            Q2=makeQuery(id+"F1.opExtrude","CAP_EDGE",EDGE,{"disambiguationData":[OSD([sQuery(id+"F0.wireOp",EDGE,"E14.4")])],"isStart":false});
            var Q3;
            Q3=makeQuery(id+"F1.opExtrude","CAP_EDGE",EDGE,{"disambiguationData":[OSD([sQuery(id+"F0.wireOp",EDGE,"E14.5")])],"isStart":false});
            var Q4;
            Q4=makeQuery(id+"F1.opExtrude","CAP_EDGE",EDGE,{"disambiguationData":[OSD([sQuery(id+"F0.wireOp",EDGE,"E14.0")])],"isStart":false});
            var Q5;
            Q5=makeQuery(id+"F1.opExtrude","CAP_EDGE",EDGE,{"disambiguationData":[OSD([sQuery(id+"F0.wireOp",EDGE,"E14.1")])],"isStart":false});
            var Q6;
            Q6=makeQuery(id+"F1.opExtrude","CAP_EDGE",EDGE,{"disambiguationData":[OSD([sQuery(id+"F0.wireOp",EDGE,"E9.1")])],"isStart":false});
            var Q7;
            Q7=makeQuery(id+"F1.opExtrude","CAP_EDGE",EDGE,{"disambiguationData":[OSD([sQuery(id+"F0.wireOp",EDGE,"E9.2")])],"isStart":false});
            var Q8;
            Q8=makeQuery(id+"F1.opExtrude","CAP_EDGE",EDGE,{"disambiguationData":[OSD([sQuery(id+"F0.wireOp",EDGE,"E9.3")])],"isStart":false});
            var Q9;
            Q9=makeQuery(id+"F1.opExtrude","CAP_EDGE",EDGE,{"disambiguationData":[OSD([sQuery(id+"F0.wireOp",EDGE,"E9.4")])],"isStart":false});
            var Q10;
            Q10=makeQuery(id+"F1.opExtrude","CAP_EDGE",EDGE,{"disambiguationData":[OSD([sQuery(id+"F0.wireOp",EDGE,"E9.5")])],"isStart":false});
            var Q11;
            Q11=makeQuery(id+"F1.opExtrude","CAP_EDGE",EDGE,{"disambiguationData":[OSD([sQuery(id+"F0.wireOp",EDGE,"E9.0")])],"isStart":false});
            var Q12;
            Q12=makeQuery(id+"F1.opExtrude","CAP_EDGE",EDGE,{"disambiguationData":[OSD([sQuery(id+"F0.wireOp",EDGE,"E10.2")])],"isStart":false});
            var Q13;
            Q13=makeQuery(id+"F1.opExtrude","CAP_EDGE",EDGE,{"disambiguationData":[OSD([sQuery(id+"F0.wireOp",EDGE,"E10.1")])],"isStart":false});
            var Q14;
            Q14=makeQuery(id+"F1.opExtrude","CAP_EDGE",EDGE,{"disambiguationData":[OSD([sQuery(id+"F0.wireOp",EDGE,"E10.0")])],"isStart":false});
            var Q15;
            Q15=makeQuery(id+"F1.opExtrude","CAP_EDGE",EDGE,{"disambiguationData":[OSD([sQuery(id+"F0.wireOp",EDGE,"E10.5")])],"isStart":false});
            var Q16;
            Q16=makeQuery(id+"F1.opExtrude","CAP_EDGE",EDGE,{"disambiguationData":[OSD([sQuery(id+"F0.wireOp",EDGE,"E10.3")])],"isStart":false});
            var Q17;
            Q17=makeQuery(id+"F1.opExtrude","CAP_EDGE",EDGE,{"disambiguationData":[OSD([sQuery(id+"F0.wireOp",EDGE,"E10.4")])],"isStart":false});
            var Q18;
            Q18=makeQuery(id+"F1.opExtrude","CAP_EDGE",EDGE,{"disambiguationData":[OSD([sQuery(id+"F0.wireOp",EDGE,"E11.1")])],"isStart":false});
            var Q19;
            Q19=makeQuery(id+"F1.opExtrude","CAP_EDGE",EDGE,{"disambiguationData":[OSD([sQuery(id+"F0.wireOp",EDGE,"E11.0")])],"isStart":false});
            var Q20;
            Q20=makeQuery(id+"F1.opExtrude","CAP_EDGE",EDGE,{"disambiguationData":[OSD([sQuery(id+"F0.wireOp",EDGE,"E11.5")])],"isStart":false});
            var Q21;
            Q21=makeQuery(id+"F1.opExtrude","CAP_EDGE",EDGE,{"disambiguationData":[OSD([sQuery(id+"F0.wireOp",EDGE,"E11.3")])],"isStart":false});
            var Q22;
            Q22=makeQuery(id+"F1.opExtrude","CAP_EDGE",EDGE,{"disambiguationData":[OSD([sQuery(id+"F0.wireOp",EDGE,"E11.2")])],"isStart":false});
            var Q23;
            Q23=makeQuery(id+"F1.opExtrude","CAP_EDGE",EDGE,{"disambiguationData":[OSD([sQuery(id+"F0.wireOp",EDGE,"E11.4")])],"isStart":false});
            var Q24;
            Q24=makeQuery(id+"F1.opExtrude","CAP_EDGE",EDGE,{"disambiguationData":[OSD([sQuery(id+"F0.wireOp",EDGE,"E13.5")])],"isStart":false});
            var Q25;
            Q25=makeQuery(id+"F1.opExtrude","CAP_EDGE",EDGE,{"disambiguationData":[OSD([sQuery(id+"F0.wireOp",EDGE,"E12.0")])],"isStart":false});
            var Q26;
            Q26=makeQuery(id+"F1.opExtrude","CAP_EDGE",EDGE,{"disambiguationData":[OSD([sQuery(id+"F0.wireOp",EDGE,"E12.5")])],"isStart":false});
            var Q27;
            Q27=makeQuery(id+"F1.opExtrude","CAP_EDGE",EDGE,{"disambiguationData":[OSD([sQuery(id+"F0.wireOp",EDGE,"E13.4")])],"isStart":false});
            var Q28;
            Q28=makeQuery(id+"F1.opExtrude","CAP_EDGE",EDGE,{"disambiguationData":[OSD([sQuery(id+"F0.wireOp",EDGE,"E13.0")])],"isStart":false});
            var Q29;
            Q29=makeQuery(id+"F1.opExtrude","CAP_EDGE",EDGE,{"disambiguationData":[OSD([sQuery(id+"F0.wireOp",EDGE,"E13.3")])],"isStart":false});
            var Q30;
            Q30=makeQuery(id+"F1.opExtrude","CAP_EDGE",EDGE,{"disambiguationData":[OSD([sQuery(id+"F0.wireOp",EDGE,"E13.2")])],"isStart":false});
            var Q31;
            Q31=makeQuery(id+"F1.opExtrude","CAP_EDGE",EDGE,{"disambiguationData":[OSD([sQuery(id+"F0.wireOp",EDGE,"E13.1")])],"isStart":false});
            var Q32;
            Q32=makeQuery(id+"F1.opExtrude","CAP_EDGE",EDGE,{"disambiguationData":[OSD([sQuery(id+"F0.wireOp",EDGE,"E12.1")])],"isStart":false});
            var Q33;
            Q33=makeQuery(id+"F1.opExtrude","CAP_EDGE",EDGE,{"disambiguationData":[OSD([sQuery(id+"F0.wireOp",EDGE,"E12.2")])],"isStart":false});
            var Q34;
            Q34=makeQuery(id+"F1.opExtrude","CAP_EDGE",EDGE,{"disambiguationData":[OSD([sQuery(id+"F0.wireOp",EDGE,"E12.3")])],"isStart":false});
            var Q35;
            Q35=makeQuery(id+"F1.opExtrude","CAP_EDGE",EDGE,{"disambiguationData":[OSD([sQuery(id+"F0.wireOp",EDGE,"E12.4")])],"isStart":false});
            var Q36;
            Q36=makeQuery(id+"F1.opExtrude","CAP_EDGE",EDGE,{"disambiguationData":[OSD([sQuery(id+"F0.wireOp",EDGE,"E14.2")])],"isStart":true});
            var Q37;
            Q37=makeQuery(id+"F1.opExtrude","CAP_EDGE",EDGE,{"disambiguationData":[OSD([sQuery(id+"F0.wireOp",EDGE,"E14.1")])],"isStart":true});
            var Q38;
            Q38=makeQuery(id+"F1.opExtrude","CAP_EDGE",EDGE,{"disambiguationData":[OSD([sQuery(id+"F0.wireOp",EDGE,"E14.0")])],"isStart":true});
            var Q39;
            Q39=makeQuery(id+"F1.opExtrude","CAP_EDGE",EDGE,{"disambiguationData":[OSD([sQuery(id+"F0.wireOp",EDGE,"E14.4")])],"isStart":true});
            var Q40;
            Q40=makeQuery(id+"F1.opExtrude","CAP_EDGE",EDGE,{"disambiguationData":[OSD([sQuery(id+"F0.wireOp",EDGE,"E14.3")])],"isStart":true});
            var Q41;
            Q41=makeQuery(id+"F1.opExtrude","CAP_EDGE",EDGE,{"disambiguationData":[OSD([sQuery(id+"F0.wireOp",EDGE,"E14.5")])],"isStart":true});
            var Q42;
            Q42=makeQuery(id+"F1.opExtrude","CAP_EDGE",EDGE,{"disambiguationData":[OSD([sQuery(id+"F0.wireOp",EDGE,"E13.0")])],"isStart":true});
            var Q43;
            Q43=makeQuery(id+"F1.opExtrude","CAP_EDGE",EDGE,{"disambiguationData":[OSD([sQuery(id+"F0.wireOp",EDGE,"E13.5")])],"isStart":true});
            var Q44;
            Q44=makeQuery(id+"F1.opExtrude","CAP_EDGE",EDGE,{"disambiguationData":[OSD([sQuery(id+"F0.wireOp",EDGE,"E13.2")])],"isStart":true});
            var Q45;
            Q45=makeQuery(id+"F1.opExtrude","CAP_EDGE",EDGE,{"disambiguationData":[OSD([sQuery(id+"F0.wireOp",EDGE,"E13.3")])],"isStart":true});
            var Q46;
            Q46=makeQuery(id+"F1.opExtrude","CAP_EDGE",EDGE,{"disambiguationData":[OSD([sQuery(id+"F0.wireOp",EDGE,"E13.1")])],"isStart":true});
            var Q47;
            Q47=makeQuery(id+"F1.opExtrude","CAP_EDGE",EDGE,{"disambiguationData":[OSD([sQuery(id+"F0.wireOp",EDGE,"E13.4")])],"isStart":true});
            var Q48;
            Q48=makeQuery(id+"F1.opExtrude","CAP_EDGE",EDGE,{"disambiguationData":[OSD([sQuery(id+"F0.wireOp",EDGE,"E9.0")])],"isStart":true});
            var Q49;
            Q49=makeQuery(id+"F1.opExtrude","CAP_EDGE",EDGE,{"disambiguationData":[OSD([sQuery(id+"F0.wireOp",EDGE,"E9.1")])],"isStart":true});
            var Q50;
            Q50=makeQuery(id+"F1.opExtrude","CAP_EDGE",EDGE,{"disambiguationData":[OSD([sQuery(id+"F0.wireOp",EDGE,"E9.2")])],"isStart":true});
            var Q51;
            Q51=makeQuery(id+"F1.opExtrude","CAP_EDGE",EDGE,{"disambiguationData":[OSD([sQuery(id+"F0.wireOp",EDGE,"E9.3")])],"isStart":true});
            var Q52;
            Q52=makeQuery(id+"F1.opExtrude","CAP_EDGE",EDGE,{"disambiguationData":[OSD([sQuery(id+"F0.wireOp",EDGE,"E9.4")])],"isStart":true});
            var Q53;
            Q53=makeQuery(id+"F1.opExtrude","CAP_EDGE",EDGE,{"disambiguationData":[OSD([sQuery(id+"F0.wireOp",EDGE,"E9.5")])],"isStart":true});
            var Q54;
            Q54=makeQuery(id+"F1.opExtrude","CAP_EDGE",EDGE,{"disambiguationData":[OSD([sQuery(id+"F0.wireOp",EDGE,"E10.5")])],"isStart":true});
            var Q55;
            Q55=makeQuery(id+"F1.opExtrude","CAP_EDGE",EDGE,{"disambiguationData":[OSD([sQuery(id+"F0.wireOp",EDGE,"E10.0")])],"isStart":true});
            var Q56;
            Q56=makeQuery(id+"F1.opExtrude","CAP_EDGE",EDGE,{"disambiguationData":[OSD([sQuery(id+"F0.wireOp",EDGE,"E10.1")])],"isStart":true});
            var Q57;
            Q57=makeQuery(id+"F1.opExtrude","CAP_EDGE",EDGE,{"disambiguationData":[OSD([sQuery(id+"F0.wireOp",EDGE,"E10.3")])],"isStart":true});
            var Q58;
            Q58=makeQuery(id+"F1.opExtrude","CAP_EDGE",EDGE,{"disambiguationData":[OSD([sQuery(id+"F0.wireOp",EDGE,"E10.4")])],"isStart":true});
            var Q59;
            Q59=makeQuery(id+"F1.opExtrude","CAP_EDGE",EDGE,{"disambiguationData":[OSD([sQuery(id+"F0.wireOp",EDGE,"E10.2")])],"isStart":true});
            var Q60;
            Q60=makeQuery(id+"F1.opExtrude","CAP_EDGE",EDGE,{"disambiguationData":[OSD([sQuery(id+"F0.wireOp",EDGE,"E11.5")])],"isStart":true});
            var Q61;
            Q61=makeQuery(id+"F1.opExtrude","CAP_EDGE",EDGE,{"disambiguationData":[OSD([sQuery(id+"F0.wireOp",EDGE,"E11.4")])],"isStart":true});
            var Q62;
            Q62=makeQuery(id+"F1.opExtrude","CAP_EDGE",EDGE,{"disambiguationData":[OSD([sQuery(id+"F0.wireOp",EDGE,"E11.3")])],"isStart":true});
            var Q63;
            Q63=makeQuery(id+"F1.opExtrude","CAP_EDGE",EDGE,{"disambiguationData":[OSD([sQuery(id+"F0.wireOp",EDGE,"E11.2")])],"isStart":true});
            var Q64;
            Q64=makeQuery(id+"F1.opExtrude","CAP_EDGE",EDGE,{"disambiguationData":[OSD([sQuery(id+"F0.wireOp",EDGE,"E11.0")])],"isStart":true});
            var Q65;
            Q65=makeQuery(id+"F1.opExtrude","CAP_EDGE",EDGE,{"disambiguationData":[OSD([sQuery(id+"F0.wireOp",EDGE,"E11.1")])],"isStart":true});
            var Q66;
            Q66=makeQuery(id+"F1.opExtrude","CAP_EDGE",EDGE,{"disambiguationData":[OSD([sQuery(id+"F0.wireOp",EDGE,"E12.3")])],"isStart":true});
            var Q67;
            Q67=makeQuery(id+"F1.opExtrude","CAP_EDGE",EDGE,{"disambiguationData":[OSD([sQuery(id+"F0.wireOp",EDGE,"E12.4")])],"isStart":true});
            var Q68;
            Q68=makeQuery(id+"F1.opExtrude","CAP_EDGE",EDGE,{"disambiguationData":[OSD([sQuery(id+"F0.wireOp",EDGE,"E12.5")])],"isStart":true});
            var Q69;
            Q69=makeQuery(id+"F1.opExtrude","CAP_EDGE",EDGE,{"disambiguationData":[OSD([sQuery(id+"F0.wireOp",EDGE,"E12.0")])],"isStart":true});
            var Q70;
            Q70=makeQuery(id+"F1.opExtrude","CAP_EDGE",EDGE,{"disambiguationData":[OSD([sQuery(id+"F0.wireOp",EDGE,"E12.1")])],"isStart":true});
            var Q71;
            Q71=makeQuery(id+"F1.opExtrude","CAP_EDGE",EDGE,{"disambiguationData":[OSD([sQuery(id+"F0.wireOp",EDGE,"E12.2")])],"isStart":true});
            fillet(context, id + "F4", {"entities" : qUnion([Q0, Q1, Q2, Q3, Q4, Q5, Q6, Q7, Q8, Q9, Q10, Q11, Q12, Q13, Q14, Q15, Q16, Q17, Q18, Q19, Q20, Q21, Q22, Q23, Q24, Q25, Q26, Q27, Q28, Q29, Q30, Q31, Q32, Q33, Q34, Q35, Q36, Q37, Q38, Q39, Q40, Q41, Q42, Q43, Q44, Q45, Q46, Q47, Q48, Q49, Q50, Q51, Q52, Q53, Q54, Q55, Q56, Q57, Q58, Q59, Q60, Q61, Q62, Q63, Q64, Q65, Q66, Q67, Q68, Q69, Q70, Q71]), "radius" : 0.5 * mm, "tangentPropagation" : true, "allowEdgeOverflow" : false});
        }
        {
            var Q0;
            {var subQ0=sQuery(id+"F0.wireOp",EDGE,"E1");var subQ1=makeQuery(id+"F0.imprint","INTERSECT",VERTEX,{"derivedFrom":[subQ0,sQuery(id+"F0.wireOp",EDGE,"E4")]});Q0=makeQuery(id+"F1.opExtrude","SWEPT_FACE",FACE,{"disambiguationData":[OSD([subQ0]),TDD([makeQuery(id+"F0.imprint","IMPRINT",EDGE,{"disambiguationData":[TD([[subQ1,1.0]])],"derivedFrom":subQ0}),makeQuery(id+"F0.imprint","IMPRINT",EDGE,{"disambiguationData":[TD([[subQ1,-1.0]])],"derivedFrom":subQ0})])]});}
            var Q1;
            {var subQ0=sQuery(id+"F0.wireOp",EDGE,"E1");var subQ1=makeQuery(id+"F0.imprint","INTERSECT",VERTEX,{"derivedFrom":[subQ0,sQuery(id+"F0.wireOp",EDGE,"E7")]});Q1=makeQuery(id+"F1.opExtrude","SWEPT_FACE",FACE,{"disambiguationData":[OSD([subQ0]),TDD([makeQuery(id+"F0.imprint","IMPRINT",EDGE,{"disambiguationData":[TD([[subQ1,1.0]])],"derivedFrom":subQ0}),makeQuery(id+"F0.imprint","IMPRINT",EDGE,{"disambiguationData":[TD([[subQ1,-1.0]])],"derivedFrom":subQ0})])]});}
            var Q2;
            {var subQ0=sQuery(id+"F0.wireOp",EDGE,"E1");var subQ1=makeQuery(id+"F0.imprint","INTERSECT",VERTEX,{"derivedFrom":[subQ0,sQuery(id+"F0.wireOp",EDGE,"E6")]});Q2=makeQuery(id+"F1.opExtrude","SWEPT_FACE",FACE,{"disambiguationData":[OSD([subQ0]),TDD([makeQuery(id+"F0.imprint","IMPRINT",EDGE,{"disambiguationData":[TD([[subQ1,1.0]])],"derivedFrom":subQ0}),makeQuery(id+"F0.imprint","IMPRINT",EDGE,{"disambiguationData":[TD([[subQ1,-1.0]])],"derivedFrom":subQ0})])]});}
            var Q3;
            {var subQ0=sQuery(id+"F0.wireOp",EDGE,"E1");var subQ1=makeQuery(id+"F0.imprint","INTERSECT",VERTEX,{"derivedFrom":[subQ0,sQuery(id+"F0.wireOp",EDGE,"E5")]});Q3=makeQuery(id+"F1.opExtrude","SWEPT_FACE",FACE,{"disambiguationData":[OSD([subQ0]),TDD([makeQuery(id+"F0.imprint","IMPRINT",EDGE,{"disambiguationData":[TD([[subQ1,1.0]])],"derivedFrom":subQ0}),makeQuery(id+"F0.imprint","IMPRINT",EDGE,{"disambiguationData":[TD([[subQ1,-1.0]])],"derivedFrom":subQ0})])]});}
            var Q4;
            {var subQ0=sQuery(id+"F0.wireOp",EDGE,"E1");var subQ1=makeQuery(id+"F0.imprint","INTERSECT",VERTEX,{"derivedFrom":[subQ0,sQuery(id+"F0.wireOp",EDGE,"E3")]});Q4=makeQuery(id+"F1.opExtrude","SWEPT_FACE",FACE,{"disambiguationData":[OSD([subQ0]),TDD([makeQuery(id+"F0.imprint","IMPRINT",EDGE,{"disambiguationData":[TD([[subQ1,1.0]])],"derivedFrom":subQ0}),makeQuery(id+"F0.imprint","IMPRINT",EDGE,{"disambiguationData":[TD([[subQ1,-1.0]])],"derivedFrom":subQ0})])]});}
            var Q5;
            {var subQ0=sQuery(id+"F0.wireOp",EDGE,"E1");var subQ1=makeQuery(id+"F0.imprint","INTERSECT",VERTEX,{"derivedFrom":[subQ0,sQuery(id+"F0.wireOp",EDGE,"E8")]});Q5=makeQuery(id+"F1.opExtrude","SWEPT_FACE",FACE,{"disambiguationData":[OSD([subQ0]),TDD([makeQuery(id+"F0.imprint","IMPRINT",EDGE,{"disambiguationData":[TD([[subQ1,1.0]])],"derivedFrom":subQ0}),makeQuery(id+"F0.imprint","IMPRINT",EDGE,{"disambiguationData":[TD([[subQ1,-1.0]])],"derivedFrom":subQ0})])]});}
            fillet(context, id + "F5", {"entities" : qUnion([Q0, Q1, Q2, Q3, Q4, Q5]), "radius" : 3 * mm, "tangentPropagation" : true, "allowEdgeOverflow" : false});
        }
        {
            var Q0;
            Q0=makeQuery(id+"F1.opExtrude","SWEPT_FACE",FACE,{"disambiguationData":[OSD([sQuery(id+"F0.wireOp",EDGE,"E35")])]});
            var Q1;
            Q1=makeQuery(id+"F1.opExtrude","SWEPT_FACE",FACE,{"disambiguationData":[OSD([sQuery(id+"F0.wireOp",EDGE,"E40")])]});
            var Q2;
            Q2=makeQuery(id+"F1.opExtrude","SWEPT_FACE",FACE,{"disambiguationData":[OSD([sQuery(id+"F0.wireOp",EDGE,"E39")])]});
            var Q3;
            Q3=makeQuery(id+"F1.opExtrude","SWEPT_FACE",FACE,{"disambiguationData":[OSD([sQuery(id+"F0.wireOp",EDGE,"E38")])]});
            var Q4;
            Q4=makeQuery(id+"F1.opExtrude","SWEPT_FACE",FACE,{"disambiguationData":[OSD([sQuery(id+"F0.wireOp",EDGE,"E36")])]});
            var Q5;
            Q5=makeQuery(id+"F1.opExtrude","SWEPT_FACE",FACE,{"disambiguationData":[OSD([sQuery(id+"F0.wireOp",EDGE,"E37")])]});
            fillet(context, id + "F6", {"entities" : qUnion([Q0, Q1, Q2, Q3, Q4, Q5]), "radius" : 1 * mm, "tangentPropagation" : true, "allowEdgeOverflow" : false});
        }
    });
